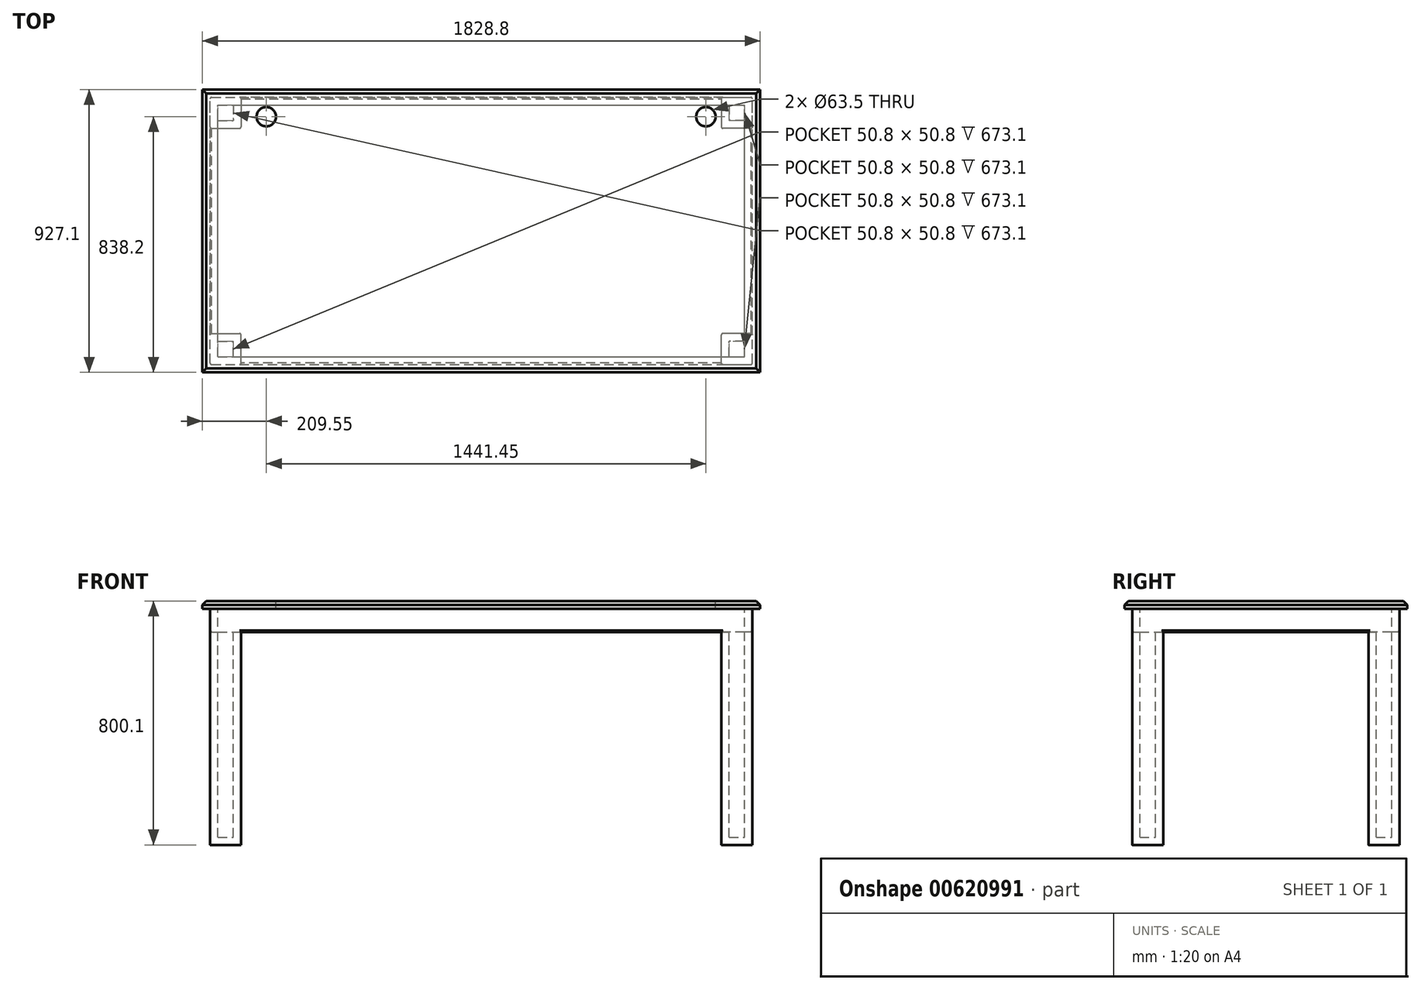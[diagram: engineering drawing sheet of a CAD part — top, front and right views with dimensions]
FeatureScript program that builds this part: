
annotation { "Feature Type Name" : "Feature", "Feature Type Description" : "" }
export const myFeature = defineFeature(function(context is Context, id is Id, definition is map)
    precondition{}
    {
        {
            var Q0;
            Q0=qCreatedBy(makeId("Top.planeOp"),FACE);
            var sketch = newSketch(context, id + "F0", { "sketchPlane" : qUnion([Q0])});
            skLineSegment(sketch, "E0.rect.bottom", {"start": v(-889, -438.15) * mm, "end": v(889, -438.15) * mm});
            skLineSegment(sketch, "E0.rect.top", {"start": v(-889, 438.15) * mm, "end": v(889, 438.15) * mm});
            skLineSegment(sketch, "E0.rect.left", {"start": v(-889, -438.15) * mm, "end": v(-889, 438.15) * mm});
            skLineSegment(sketch, "E0.rect.right", {"start": v(889, -438.15) * mm, "end": v(889, 438.15) * mm});
            skPoint(sketch, "E0.rect.middle", {"position": v(0, 0) * mm});
            skSolve(sketch);
        }
        {
            var Q0;
            Q0=qCreatedBy(makeId("Top.planeOp"),FACE);
            var sketch = newSketch(context, id + "F1", { "sketchPlane" : qUnion([Q0])});
            skLineSegment(sketch, "E1.rect.bottom", {"start": v(-914.4, 463.55) * mm, "end": v(914.4, 463.55) * mm});
            skLineSegment(sketch, "E1.rect.top", {"start": v(-914.4, -463.55) * mm, "end": v(914.4, -463.55) * mm});
            skLineSegment(sketch, "E1.rect.left", {"start": v(-914.4, 463.55) * mm, "end": v(-914.4, -463.55) * mm});
            skLineSegment(sketch, "E1.rect.right", {"start": v(914.4, 463.55) * mm, "end": v(914.4, -463.55) * mm});
            skPoint(sketch, "E1.rect.middle", {"position": v(0, 0) * mm});
            skSolve(sketch);
        }
        {
            var Q0;
            Q0=qSketchRegion(id+"F1",true);
            extrude(context, id + "F2", {"entities" : qUnion([Q0]), "oppositeDirection" : true, "depth" : 25.4 * mm});
        }
        {
            var Q0;
            Q0=qSketchRegion(id+"F0",true);
            extrude(context, id + "F3", {"entities" : qUnion([Q0]), "operationType" : NewBodyOperationType.ADD, "oppositeDirection" : true, "depth" : 101.6 * mm});
        }
        {
            var Q0;
            Q0=makeQuery(id+"F3.opExtrude","CAP_FACE",FACE,{"disambiguationData":[OSD([sQuery(id+"F0.wireOp",EDGE,"E0.rect.bottom"),sQuery(id+"F0.wireOp",EDGE,"E0.rect.top"),sQuery(id+"F0.wireOp",EDGE,"E0.rect.left"),sQuery(id+"F0.wireOp",EDGE,"E0.rect.right")])],"isStart":false});
            var sketch = newSketch(context, id + "F4", { "sketchPlane" : qUnion([Q0])});
            skLineSegment(sketch, "E2.bottom", {"start": v(-889, 438.15) * mm, "end": v(-787.4, 438.15) * mm});
            skLineSegment(sketch, "E2.top", {"start": v(-889, 336.55) * mm, "end": v(-787.4, 336.55) * mm});
            skLineSegment(sketch, "E2.left", {"start": v(-889, 438.15) * mm, "end": v(-889, 336.55) * mm});
            skLineSegment(sketch, "E2.right", {"start": v(-787.4, 438.15) * mm, "end": v(-787.4, 336.55) * mm});
            skLineSegment(sketch, "E3.bottom", {"start": v(889, -438.15) * mm, "end": v(787.4, -438.15) * mm});
            skLineSegment(sketch, "E3.top", {"start": v(889, -336.55) * mm, "end": v(787.4, -336.55) * mm});
            skLineSegment(sketch, "E3.left", {"start": v(889, -438.15) * mm, "end": v(889, -336.55) * mm});
            skLineSegment(sketch, "E3.right", {"start": v(787.4, -438.15) * mm, "end": v(787.4, -336.55) * mm});
            skLineSegment(sketch, "E4.bottom", {"start": v(889, 438.15) * mm, "end": v(787.4, 438.15) * mm});
            skLineSegment(sketch, "E4.top", {"start": v(889, 336.55) * mm, "end": v(787.4, 336.55) * mm});
            skLineSegment(sketch, "E4.left", {"start": v(889, 438.15) * mm, "end": v(889, 336.55) * mm});
            skLineSegment(sketch, "E4.right", {"start": v(787.4, 438.15) * mm, "end": v(787.4, 336.55) * mm});
            skLineSegment(sketch, "E5.bottom", {"start": v(-889, -438.15) * mm, "end": v(-787.4, -438.15) * mm});
            skLineSegment(sketch, "E5.top", {"start": v(-889, -336.55) * mm, "end": v(-787.4, -336.55) * mm});
            skLineSegment(sketch, "E5.left", {"start": v(-889, -438.15) * mm, "end": v(-889, -336.55) * mm});
            skLineSegment(sketch, "E5.right", {"start": v(-787.4, -438.15) * mm, "end": v(-787.4, -336.55) * mm});
            skSolve(sketch);
        }
        {
            var Q0;
            Q0=makeQuery(id+"F4.imprint","IMPRINT",FACE,{"disambiguationData":[TD([[makeQuery(id+"F4.imprint","IMPRINT",EDGE,{"derivedFrom":sQuery(id+"F4.wireOp",EDGE,"E2.bottom")}),-1.0]])]});
            var Q1;
            Q1=makeQuery(id+"F4.imprint","IMPRINT",FACE,{"disambiguationData":[TD([[makeQuery(id+"F4.imprint","IMPRINT",EDGE,{"derivedFrom":sQuery(id+"F4.wireOp",EDGE,"E5.bottom")}),1.0]])]});
            var Q2;
            Q2=makeQuery(id+"F4.imprint","IMPRINT",FACE,{"disambiguationData":[TD([[makeQuery(id+"F4.imprint","IMPRINT",EDGE,{"derivedFrom":sQuery(id+"F4.wireOp",EDGE,"E4.bottom")}),-1.0]])]});
            var Q3;
            Q3=makeQuery(id+"F4.imprint","IMPRINT",FACE,{"disambiguationData":[TD([[makeQuery(id+"F4.imprint","IMPRINT",EDGE,{"derivedFrom":sQuery(id+"F4.wireOp",EDGE,"E3.bottom")}),1.0]])]});
            extrude(context, id + "F5", {"entities" : qUnion([Q0, Q1, Q2, Q3]), "operationType" : NewBodyOperationType.ADD, "depth" : 698.5 * mm});
        }
        {
            var Q0;
            Q0=makeQuery(id+"F3.opExtrude","CAP_FACE",FACE,{"disambiguationData":[OSD([sQuery(id+"F0.wireOp",EDGE,"E0.rect.bottom"),sQuery(id+"F0.wireOp",EDGE,"E0.rect.top"),sQuery(id+"F0.wireOp",EDGE,"E0.rect.left"),sQuery(id+"F0.wireOp",EDGE,"E0.rect.right")])],"isStart":false});
            shell(context, id + "F6", {"entities" : qUnion([Q0]), "thickness" : 25.4 * mm});
        }
        {
            var Q0;
            Q0=makeQuery(id+"F2.opExtrude","CAP_FACE",FACE,{"disambiguationData":[OSD([sQuery(id+"F1.wireOp",EDGE,"E1.rect.bottom"),sQuery(id+"F1.wireOp",EDGE,"E1.rect.top"),sQuery(id+"F1.wireOp",EDGE,"E1.rect.left"),sQuery(id+"F1.wireOp",EDGE,"E1.rect.right")])],"isStart":true});
            var sketch = newSketch(context, id + "F7", { "sketchPlane" : qUnion([Q0])});
            skCircle(sketch, "E6", {"center": v(-704.85, 374.65) * mm, "radius": 31.75 * mm});
            skCircle(sketch, "E7", {"center": v(736.6, 374.65) * mm, "radius": 31.75 * mm});
            skSolve(sketch);
        }
        {
            var Q0;
            Q0=makeQuery(id+"F7.imprint","IMPRINT",FACE,{"disambiguationData":[TD([[makeQuery(id+"F7.imprint","IMPRINT",EDGE,{"derivedFrom":sQuery(id+"F7.wireOp",EDGE,"E6")}),1.0]])]});
            var Q1;
            Q1=makeQuery(id+"F7.imprint","IMPRINT",FACE,{"disambiguationData":[TD([[makeQuery(id+"F7.imprint","IMPRINT",EDGE,{"derivedFrom":sQuery(id+"F7.wireOp",EDGE,"E7")}),1.0]])]});
            extrude(context, id + "F8", {"entities" : qUnion([Q0, Q1]), "operationType" : NewBodyOperationType.REMOVE, "oppositeDirection" : true, "depth" : 25.4 * mm});
        }
        {
            var Q0;
            Q0=makeQuery(id+"F2.opExtrude","CAP_EDGE",EDGE,{"disambiguationData":[OSD([sQuery(id+"F1.wireOp",EDGE,"E1.rect.top")])],"isStart":true});
            var Q1;
            Q1=makeQuery(id+"F2.opExtrude","CAP_EDGE",EDGE,{"disambiguationData":[OSD([sQuery(id+"F1.wireOp",EDGE,"E1.rect.left")])],"isStart":true});
            var Q2;
            Q2=makeQuery(id+"F2.opExtrude","CAP_EDGE",EDGE,{"disambiguationData":[OSD([sQuery(id+"F1.wireOp",EDGE,"E1.rect.bottom")])],"isStart":true});
            var Q3;
            Q3=makeQuery(id+"F2.opExtrude","CAP_EDGE",EDGE,{"disambiguationData":[OSD([sQuery(id+"F1.wireOp",EDGE,"E1.rect.right")])],"isStart":true});
            chamfer(context, id + "F9", {"entities" : qUnion([Q0, Q1, Q2, Q3]), "width" : 12.7 * mm, "tangentPropagation" : true});
        }
        {
            var Q0;
            Q0=makeQuery(id+"F5.boolean.opBoolean","MERGE",EDGE,{"derivedFrom":[makeQuery(id+"F3.opExtrude","SWEPT_EDGE",EDGE,{"disambiguationData":[OSD([sQuery(id+"F0.wireOp",EDGE,"E0.rect.bottom"),sQuery(id+"F0.wireOp",EDGE,"E0.rect.left")])]}),makeQuery(id+"F5.opExtrude","SWEPT_EDGE",EDGE,{"disambiguationData":[OSD([sQuery(id+"F4.wireOp",EDGE,"E2.bottom"),sQuery(id+"F4.wireOp",EDGE,"E2.left")])]})]});
            var Q1;
            Q1=makeQuery(id+"F5.opExtrude","SWEPT_EDGE",EDGE,{"disambiguationData":[OSD([sQuery(id+"F0.wireOp",EDGE,"E0.rect.bottom"),sQuery(id+"F4.wireOp",EDGE,"E2.bottom"),sQuery(id+"F4.wireOp",EDGE,"E2.right")])]});
            var Q2;
            Q2=makeQuery(id+"F5.opExtrude","SWEPT_EDGE",EDGE,{"disambiguationData":[OSD([sQuery(id+"F0.wireOp",EDGE,"E0.rect.left"),sQuery(id+"F4.wireOp",EDGE,"E2.top"),sQuery(id+"F4.wireOp",EDGE,"E2.left")])]});
            var Q3;
            Q3=makeQuery(id+"F5.opExtrude","SWEPT_EDGE",EDGE,{"disambiguationData":[OSD([sQuery(id+"F4.wireOp",EDGE,"E2.top"),sQuery(id+"F4.wireOp",EDGE,"E2.right")])]});
            var Q4;
            Q4=makeQuery(id+"F5.opExtrude","SWEPT_EDGE",EDGE,{"disambiguationData":[OSD([sQuery(id+"F0.wireOp",EDGE,"E0.rect.bottom"),sQuery(id+"F4.wireOp",EDGE,"E4.bottom"),sQuery(id+"F4.wireOp",EDGE,"E4.right")])]});
            var Q5;
            Q5=makeQuery(id+"F5.boolean.opBoolean","MERGE",EDGE,{"derivedFrom":[makeQuery(id+"F3.opExtrude","SWEPT_EDGE",EDGE,{"disambiguationData":[OSD([sQuery(id+"F0.wireOp",EDGE,"E0.rect.bottom"),sQuery(id+"F0.wireOp",EDGE,"E0.rect.right")])]}),makeQuery(id+"F5.opExtrude","SWEPT_EDGE",EDGE,{"disambiguationData":[OSD([sQuery(id+"F4.wireOp",EDGE,"E4.bottom"),sQuery(id+"F4.wireOp",EDGE,"E4.left")])]})]});
            var Q6;
            Q6=makeQuery(id+"F5.opExtrude","SWEPT_EDGE",EDGE,{"disambiguationData":[OSD([sQuery(id+"F4.wireOp",EDGE,"E4.top"),sQuery(id+"F4.wireOp",EDGE,"E4.right")])]});
            var Q7;
            Q7=makeQuery(id+"F5.opExtrude","SWEPT_EDGE",EDGE,{"disambiguationData":[OSD([sQuery(id+"F0.wireOp",EDGE,"E0.rect.right"),sQuery(id+"F4.wireOp",EDGE,"E4.top"),sQuery(id+"F4.wireOp",EDGE,"E4.left")])]});
            var Q8;
            Q8=makeQuery(id+"F5.opExtrude","SWEPT_EDGE",EDGE,{"disambiguationData":[OSD([sQuery(id+"F0.wireOp",EDGE,"E0.rect.right"),sQuery(id+"F4.wireOp",EDGE,"E3.top"),sQuery(id+"F4.wireOp",EDGE,"E3.left")])]});
            var Q9;
            Q9=makeQuery(id+"F5.opExtrude","SWEPT_EDGE",EDGE,{"disambiguationData":[OSD([sQuery(id+"F4.wireOp",EDGE,"E3.top"),sQuery(id+"F4.wireOp",EDGE,"E3.right")])]});
            var Q10;
            Q10=makeQuery(id+"F5.boolean.opBoolean","MERGE",EDGE,{"derivedFrom":[makeQuery(id+"F3.opExtrude","SWEPT_EDGE",EDGE,{"disambiguationData":[OSD([sQuery(id+"F0.wireOp",EDGE,"E0.rect.top"),sQuery(id+"F0.wireOp",EDGE,"E0.rect.right")])]}),makeQuery(id+"F5.opExtrude","SWEPT_EDGE",EDGE,{"disambiguationData":[OSD([sQuery(id+"F4.wireOp",EDGE,"E3.bottom"),sQuery(id+"F4.wireOp",EDGE,"E3.left")])]})]});
            var Q11;
            Q11=makeQuery(id+"F5.opExtrude","SWEPT_EDGE",EDGE,{"disambiguationData":[OSD([sQuery(id+"F0.wireOp",EDGE,"E0.rect.top"),sQuery(id+"F4.wireOp",EDGE,"E3.bottom"),sQuery(id+"F4.wireOp",EDGE,"E3.right")])]});
            var Q12;
            Q12=makeQuery(id+"F5.boolean.opBoolean","MERGE",EDGE,{"derivedFrom":[makeQuery(id+"F3.opExtrude","SWEPT_EDGE",EDGE,{"disambiguationData":[OSD([sQuery(id+"F0.wireOp",EDGE,"E0.rect.top"),sQuery(id+"F0.wireOp",EDGE,"E0.rect.left")])]}),makeQuery(id+"F5.opExtrude","SWEPT_EDGE",EDGE,{"disambiguationData":[OSD([sQuery(id+"F4.wireOp",EDGE,"E5.bottom"),sQuery(id+"F4.wireOp",EDGE,"E5.left")])]})]});
            var Q13;
            Q13=makeQuery(id+"F5.opExtrude","SWEPT_EDGE",EDGE,{"disambiguationData":[OSD([sQuery(id+"F0.wireOp",EDGE,"E0.rect.top"),sQuery(id+"F4.wireOp",EDGE,"E5.bottom"),sQuery(id+"F4.wireOp",EDGE,"E5.right")])]});
            var Q14;
            Q14=makeQuery(id+"F5.opExtrude","SWEPT_EDGE",EDGE,{"disambiguationData":[OSD([sQuery(id+"F0.wireOp",EDGE,"E0.rect.left"),sQuery(id+"F4.wireOp",EDGE,"E5.top"),sQuery(id+"F4.wireOp",EDGE,"E5.left")])]});
            var Q15;
            Q15=makeQuery(id+"F5.opExtrude","SWEPT_EDGE",EDGE,{"disambiguationData":[OSD([sQuery(id+"F4.wireOp",EDGE,"E5.top"),sQuery(id+"F4.wireOp",EDGE,"E5.right")])]});
            fillet(context, id + "F10", {"entities" : qUnion([Q0, Q1, Q2, Q3, Q4, Q5, Q6, Q7, Q8, Q9, Q10, Q11, Q12, Q13, Q14, Q15]), "radius" : 5.08 * mm, "tangentPropagation" : true, "allowEdgeOverflow" : false});
        }
        {
            var Q0;
            Q0=makeQuery(id+"F3.opExtrude","CAP_EDGE",EDGE,{"disambiguationData":[OSD([sQuery(id+"F0.wireOp",EDGE,"E0.rect.left")])],"isStart":false});
            var Q1;
            Q1=makeQuery(id+"F3.opExtrude","CAP_EDGE",EDGE,{"disambiguationData":[OSD([sQuery(id+"F0.wireOp",EDGE,"E0.rect.bottom")])],"isStart":false});
            var Q2;
            Q2=makeQuery(id+"F3.opExtrude","CAP_EDGE",EDGE,{"disambiguationData":[OSD([sQuery(id+"F0.wireOp",EDGE,"E0.rect.right")])],"isStart":false});
            var Q3;
            Q3=makeQuery(id+"F3.opExtrude","CAP_EDGE",EDGE,{"disambiguationData":[OSD([sQuery(id+"F0.wireOp",EDGE,"E0.rect.top")])],"isStart":false});
            chamfer(context, id + "F11", {"entities" : qUnion([Q0, Q1, Q2, Q3]), "width" : 5.08 * mm, "tangentPropagation" : true});
        }
    });
